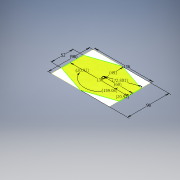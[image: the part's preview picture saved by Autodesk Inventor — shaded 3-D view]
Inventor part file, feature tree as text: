
AUTODESK INVENTOR PART (.ipt)
format: ipt  version: 2016 (Build 200138000, 138)  size: 110,592 bytes
history: native  units: mm
features: sketch x1, other x1
ambient origin geometry x8: Origin, YZ Plane, XZ Plane, XY Plane, X Axis, Y Axis, Z Axis, Center Point
feature tree (2):
  sketch  "Sketch1"  dims[d1=136.0mm d2=98.0mm d6=136.0mm d7=98.000008mm d18=52.0mm d28=3.652014mm d29=3.652014mm d30=27.763911mm d32=68.0mm d33=72.801099mm d34=49.0mm]
  other  "Image1"
